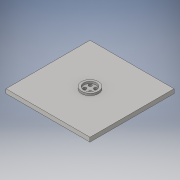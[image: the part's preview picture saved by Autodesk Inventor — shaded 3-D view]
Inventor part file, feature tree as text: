
AUTODESK INVENTOR PART (.ipt)
format: ipt  version: 2016 (Build 200138000, 138)  size: 119,808 bytes
history: native  units: in
note: dims shown in document units (in); Inventor stores cm internally (conversion verified against a paired STEP export)
features: hole x4, sketch x3, extrude x2
ambient origin geometry x8: Origin, YZ Plane, XZ Plane, XY Plane, X Axis, Y Axis, Z Axis, Center Point
bodies: Solid1 (feature_tree)
feature tree (9):
  extrude  "Extrusion1"  Depth=5.0in
  extrude  "Extrusion2"  Depth=0.118in TaperAngle=0.0deg
  sketch  "Sketch3"  dims[d9=1.0in d10=1.0in d11=0.19in d12=0.75in d13=0.375in d14=0.25in d15=0.5635in d16=1.0in d17=0.8108in d18=1.0in d19=1.0in d20=0.19in d21=0.75in d22=0.375in d23=0.25in d24=0.5635in d25=1.0in d26=0.8108in d27=1.0in d28=1.0in d29=0.19in d30=0.75in d31=0.375in d32=0.25in d33=0.5635in d34=1.0in d35=0.8108in d36=0.19in d37=0.75in d38=0.375in d39=0.25in d40=0.5635in d41=1.0in d42=0.8108in]
  hole  "Hole1"  [1 undecoded]
  hole  "Hole2"  [1 undecoded]
  hole  "Hole3"  [1 undecoded]
  hole  "Hole4"  [1 undecoded]
  sketch  "Sketch1"  dims[d0=5.0in d1=5.0in]
  sketch  "Sketch2"  dims[d2=0.25in d3=0.0in d5=0.118in d6=0.0in]
note: 4 required parameter values undecoded (feature->parameter linkage not recoverable at this tier; creation-order binding heuristic only, values carry confidence <= 0.55)
